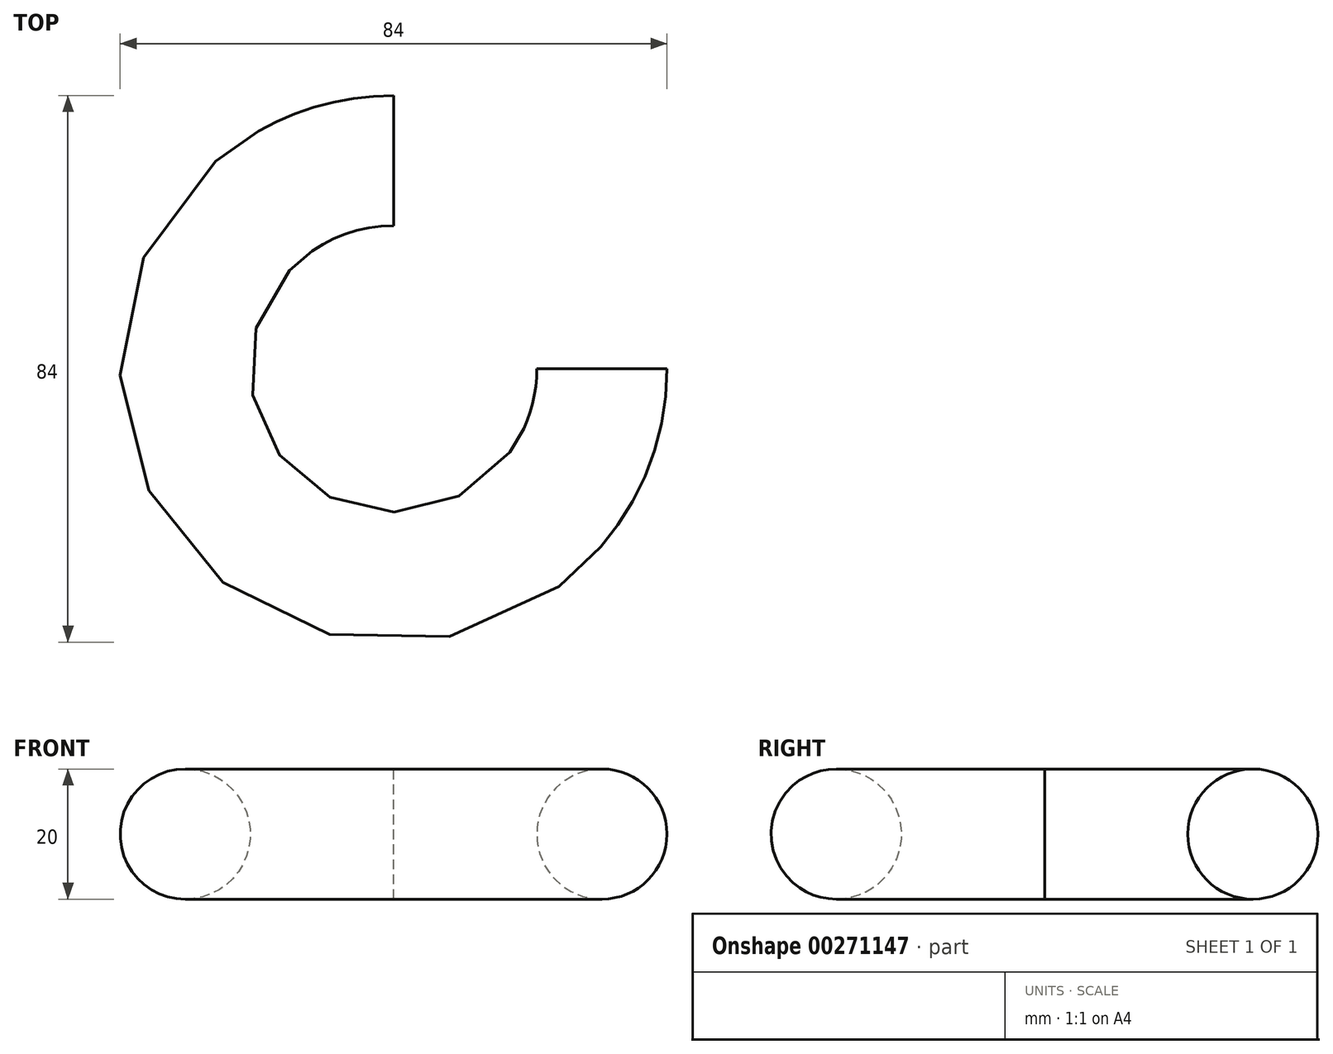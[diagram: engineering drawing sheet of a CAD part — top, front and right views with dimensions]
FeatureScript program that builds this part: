
annotation { "Feature Type Name" : "Feature", "Feature Type Description" : "" }
export const myFeature = defineFeature(function(context is Context, id is Id, definition is map)
    precondition{}
    {
        {
            var Q0;
            Q0=qCreatedBy(makeId("Front.planeOp"),FACE);
            var sketch = newSketch(context, id + "F0", { "sketchPlane" : qUnion([Q0])});
            skPoint(sketch, "E0.center.orphan", {"position": v(226.51, 0) * mm});
            skCircle(sketch, "E1", {"center": v(32, 0) * mm, "radius": 10 * mm});
            skLineSegment(sketch, "E2", {"start": v(0, 37.75) * mm, "end": v(0, -54.07) * mm, "construction": true});
            skSolve(sketch);
        }
        {
            var Q0;
            Q0=makeQuery(id+"F0.imprint","IMPRINT",FACE,{"disambiguationData":[TD([[makeQuery(id+"F0.imprint","IMPRINT",EDGE,{"derivedFrom":sQuery(id+"F0.wireOp",EDGE,"E1")}),1.0]])]});
            var Q1;
            Q1=sQuery(id+"F0.wireOp",EDGE,"E2");
            revolve(context, id + "F1", {"entities" : qUnion([Q0]), "axis" : qUnion([Q1]), "revolveType" : RevolveType.ONE_DIRECTION, "angle" : 270 * degree});
        }
    });
